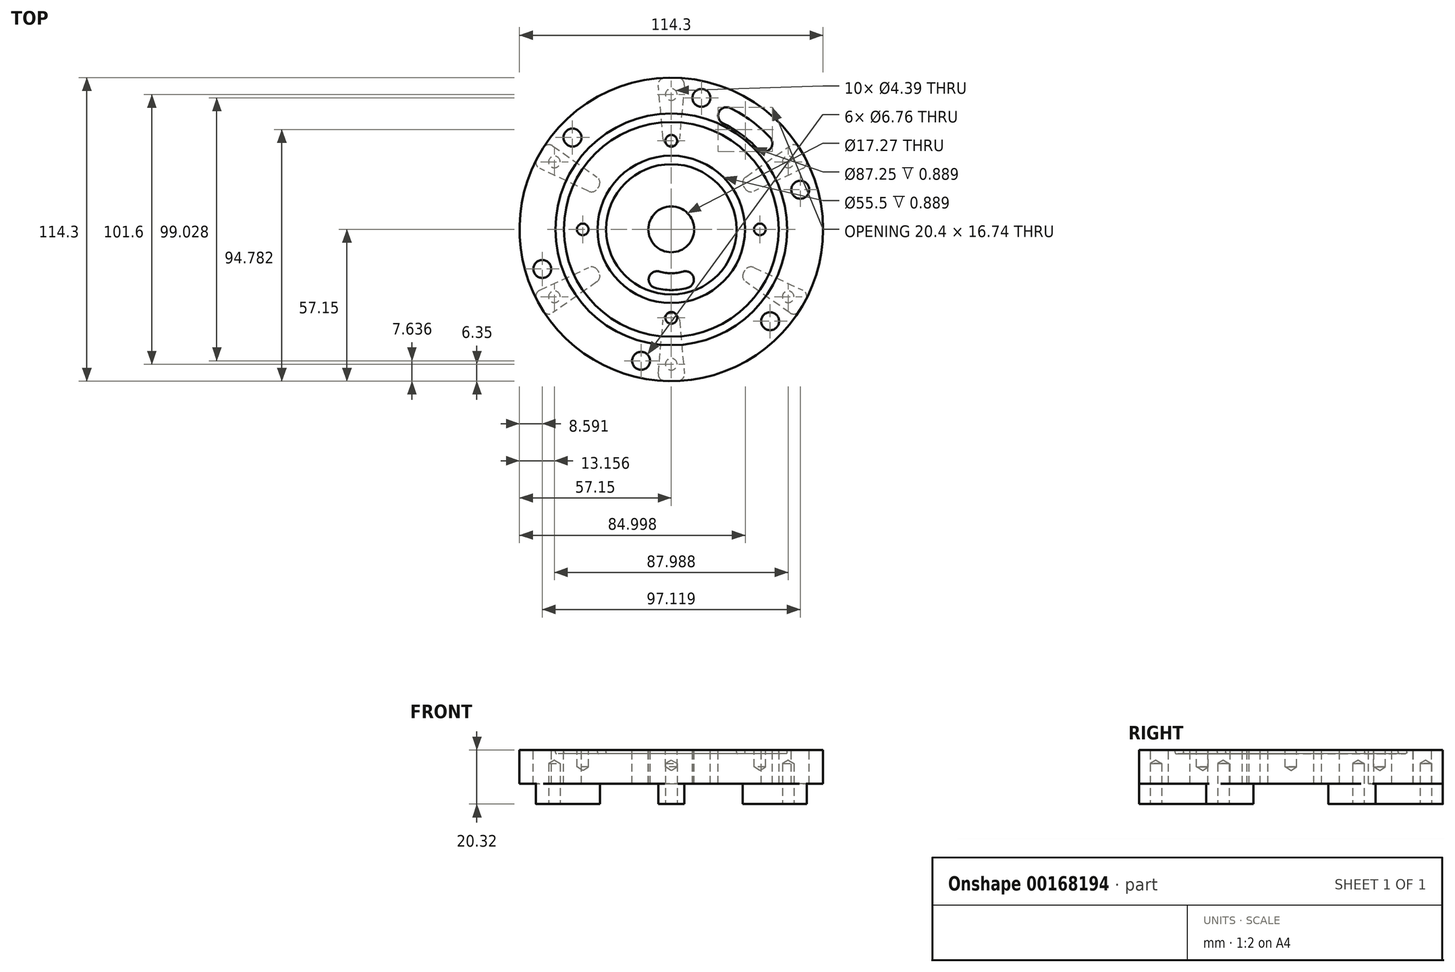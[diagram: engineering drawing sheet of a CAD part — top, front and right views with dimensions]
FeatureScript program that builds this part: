
annotation { "Feature Type Name" : "Feature", "Feature Type Description" : "" }
export const myFeature = defineFeature(function(context is Context, id is Id, definition is map)
    precondition{}
    {
        {
            var Q0;
            Q0=qCreatedBy(makeId("Top.planeOp"),FACE);
            var sketch = newSketch(context, id + "F0", { "sketchPlane" : qUnion([Q0])});
            skCircle(sketch, "E0", {"center": v(0, 0) * mm, "radius": 57.15 * mm});
            skSolve(sketch);
        }
        {
            var Q0;
            Q0=makeQuery(id+"F0.imprint","IMPRINT",FACE,{"disambiguationData":[TD([[makeQuery(id+"F0.imprint","IMPRINT",EDGE,{"derivedFrom":sQuery(id+"F0.wireOp",EDGE,"E0")}),1.0]])]});
            extrude(context, id + "F1", {"entities" : qUnion([Q0]), "depth" : 12.7 * mm});
        }
        {
            var Q0;
            Q0=makeQuery(id+"FNZgXB3MDCEPfWC_1.boolean.opBoolean","SPLIT",FACE,{"disambiguationData":[TD([makeQuery(id+"FNZgXB3MDCEPfWC_1.opExtrude","SWEPT_FACE",FACE,{"disambiguationData":[OSD([sQuery(id+"FiLk9hSRQ8Dv81E_1.wireOp",EDGE,"Xvq2NHEn-EDZK-GzOR-rNrk-moL4fFsD4KvI")])]})])],"derivedFrom":makeQuery(id+"F1.opExtrude","CAP_FACE",FACE,{"disambiguationData":[OSD([sQuery(id+"F0.wireOp",EDGE,"E0")])],"isStart":false})});
            var sketch = newSketch(context, id + "F2", { "sketchPlane" : qUnion([Q0])});
            skCircle(sketch, "E1", {"center": v(0, 0) * mm, "radius": 8.64 * mm});
            skSolve(sketch);
        }
        {
            var Q0;
            Q0 = qSketchRegion(id + "F2", true);
            extrude(context, id + "F3", {"entities" : qUnion([Q0]), "operationType" : NewBodyOperationType.REMOVE, "endBound" : BoundingType.THROUGH_ALL, "oppositeDirection" : true, "depth" : 25.4 * mm});
        }
        {
            var Q0;
            Q0=makeQuery(id+"F1.opExtrude","CAP_FACE",FACE,{"disambiguationData":[OSD([sQuery(id+"F0.wireOp",EDGE,"E0")])],"isStart":true});
            var sketch = newSketch(context, id + "F4", { "sketchPlane" : qUnion([Q0])});
            skArc(sketch, "E2", {"start": v(-5.14, -56.92) * mm, "mid": v(0, -57.15) * mm, "end": v(5.14, -56.92) * mm});
            skArc(sketch, "E3", {"start": v(-2.86, -31.62) * mm, "mid": v(0, -31.75) * mm, "end": v(2.86, -31.62) * mm});
            skLineSegment(sketch, "E4", {"start": v(0, 0) * mm, "end": v(2.86, -31.62) * mm, "construction": true});
            skLineSegment(sketch, "E5", {"start": v(5.14, -56.92) * mm, "end": v(2.86, -31.62) * mm});
            skLineSegment(sketch, "E6", {"start": v(-2.86, -31.62) * mm, "end": v(-5.14, -56.92) * mm});
            skLineSegment(sketch, "E7", {"start": v(-2.86, -31.62) * mm, "end": v(2.86, -31.62) * mm, "construction": true});
            skPoint(sketch, "E8", {"position": v(0, -31.62) * mm});
            skLineSegment(sketch, "E9", {"start": v(0, 0) * mm, "end": v(-2.86, -31.62) * mm, "construction": true});
            skSolve(sketch);
        }
        {
            var Q0;
            Q0 = qSketchRegion(id + "F4", true);
            extrude(context, id + "F5", {"entities" : qUnion([Q0]), "operationType" : NewBodyOperationType.ADD, "depth" : 7.62 * mm});
        }
        {
            var Q0;
            Q0=makeQuery(id+"F5.opExtrude","SWEPT_EDGE",EDGE,{"disambiguationData":[OSD([sQuery(id+"F0.wireOp",EDGE,"E0"),sQuery(id+"F4.wireOp",EDGE,"E2"),sQuery(id+"F4.wireOp",EDGE,"E5")])]});
            var Q1;
            Q1=makeQuery(id+"F5.opExtrude","SWEPT_EDGE",EDGE,{"disambiguationData":[OSD([sQuery(id+"F4.wireOp",EDGE,"E3"),sQuery(id+"F4.wireOp",EDGE,"E5")])]});
            var Q2;
            Q2=makeQuery(id+"F5.opExtrude","SWEPT_EDGE",EDGE,{"disambiguationData":[OSD([sQuery(id+"F0.wireOp",EDGE,"E0"),sQuery(id+"F4.wireOp",EDGE,"E2"),sQuery(id+"F4.wireOp",EDGE,"sxsrdx0H-xiQs-OsdF-6Z6r-2XBd8uqwUAgb")])]});
            var Q3;
            Q3=makeQuery(id+"F5.opExtrude","SWEPT_EDGE",EDGE,{"disambiguationData":[OSD([sQuery(id+"F4.wireOp",EDGE,"E3"),sQuery(id+"F4.wireOp",EDGE,"sxsrdx0H-xiQs-OsdF-6Z6r-2XBd8uqwUAgb")])]});
            fillet(context, id + "F6", {"entities" : qUnion([Q0, Q1, Q2, Q3]), "radius" : 2.54 * mm, "tangentPropagation" : true, "allowEdgeOverflow" : false});
        }
        {
            var Q0;
            Q0=makeQuery(id+"F5.opExtrude","CAP_FACE",FACE,{"disambiguationData":[OSD([sQuery(id+"F4.wireOp",EDGE,"E2"),sQuery(id+"F4.wireOp",EDGE,"E3"),sQuery(id+"F4.wireOp",EDGE,"E5"),sQuery(id+"F4.wireOp",EDGE,"sxsrdx0H-xiQs-OsdF-6Z6r-2XBd8uqwUAgb")])],"isStart":false});
            var sketch = newSketch(context, id + "F7", { "sketchPlane" : qUnion([Q0])});
            skPoint(sketch, "E10", {"position": v(0, -17.36) * mm});
            skLineSegment(sketch, "E11", {"start": v(0, 0) * mm, "end": v(0, -17.36) * mm, "construction": true});
            skLineSegment(sketch, "E12", {"start": v(0, -17.36) * mm, "end": v(0, -57.1) * mm, "construction": true});
            skPoint(sketch, "E13.3.0", {"position": v(0, -50.8) * mm});
            skPoint(sketch, "E13.center", {"position": v(0, 0) * mm});
            skPoint(sketch, "E14.1.0", {"position": v(44, -25.4) * mm});
            skPoint(sketch, "E14.2.0", {"position": v(44, 25.4) * mm});
            skPoint(sketch, "E15.0.3.0", {"position": v(0, 50.8) * mm});
            skPoint(sketch, "E15.0.4.0", {"position": v(-44, 25.4) * mm});
            skPoint(sketch, "E15.0.5.0", {"position": v(-44, -25.4) * mm});
            skSolve(sketch);
        }
        {
            var Q0;
            Q0=makeQuery(id+"F1.opExtrude","SWEPT_BODY",BODY,{"disambiguationData":[OSD([sQuery(id+"F0.wireOp",EDGE,"E0")])]});
            var Q1;
            Q1=makeQuery(id+"F3.boolean.opBoolean","COPY",FACE,{"derivedFrom":makeQuery(id+"F3.opExtrude","SWEPT_FACE",FACE,{"disambiguationData":[OSD([sQuery(id+"F2.wireOp",EDGE,"E1")])]})});
            circularPattern(context, id + "F8", {"operationType" : NewBodyOperationType.ADD, "entities" : qUnion([Q0]), "axis" : qUnion([Q1]), "angle" : 360 * degree, "instanceCount" : 6, "equalSpace" : true});
        }
        {
            var Q0;
            Q0=sQuery(id+"F7.wireOp",VERTEX,"E13.3.0");
            var Q1;
            Q1=sQuery(id+"F7.wireOp",VERTEX,"E14.1.0");
            var Q2;
            Q2=sQuery(id+"F7.wireOp",VERTEX,"E14.2.0");
            var Q3;
            Q3=sQuery(id+"F7.wireOp",VERTEX,"E15.0.3.0");
            var Q4;
            Q4=sQuery(id+"F7.wireOp",VERTEX,"E15.0.4.0");
            var Q5;
            Q5=sQuery(id+"F7.wireOp",VERTEX,"E15.0.5.0");
            var Q6;
            Q6=makeQuery(id+"F1.opExtrude","SWEPT_BODY",BODY,{"disambiguationData":[OSD([sQuery(id+"F0.wireOp",EDGE,"E0")])]});
            hole(context, id + "F9", {"style" : HoleStyle.SIMPLE, "endStyle" : HoleEndStyle.BLIND, "holeDiameter" : 4.4 * mm, "holeDepth" : 15.24 * mm, "locations" : qUnion([Q0, Q1, Q2, Q3, Q4, Q5]), "scope" : qUnion([Q6])});
        }
        {
            var Q0;
            {var subQ0=sQuery(id+"F0.wireOp",EDGE,"E0");Q0=makeQuery(id+"FNZgXB3MDCEPfWC_1.boolean.opBoolean","SPLIT",FACE,{"disambiguationData":[TD([makeQuery(id+"F1.opExtrude","SWEPT_FACE",FACE,{"disambiguationData":[OSD([subQ0])]})])],"derivedFrom":makeQuery(id+"F1.opExtrude","CAP_FACE",FACE,{"disambiguationData":[OSD([subQ0])],"isStart":false})});}
            var sketch = newSketch(context, id + "F10", { "sketchPlane" : qUnion([Q0])});
            skCircle(sketch, "E16", {"center": v(0, 0) * mm, "radius": 42.02 * mm, "construction": true});
            skCircle(sketch, "E17", {"center": v(0, 0) * mm, "radius": 40.42 * mm});
            skCircle(sketch, "E18", {"center": v(0, 0) * mm, "radius": 43.62 * mm});
            skSolve(sketch);
        }
        {
            var Q0;
            Q0 = qSketchRegion(id + "F10", true);
            extrude(context, id + "F11", {"entities" : qUnion([Q0]), "operationType" : NewBodyOperationType.REMOVE, "oppositeDirection" : true, "depth" : 1.3 * mm});
        }
        {
            var Q0;
            Q0=makeQuery(id+"F11.boolean.opBoolean","COPY",EDGE,{"derivedFrom":makeQuery(id+"F11.opExtrude","CAP_EDGE",EDGE,{"disambiguationData":[OSD([sQuery(id+"F10.wireOp",EDGE,"E18")])],"isStart":false})});
            var Q1;
            Q1=makeQuery(id+"F11.boolean.opBoolean","COPY",EDGE,{"derivedFrom":makeQuery(id+"F11.opExtrude","CAP_EDGE",EDGE,{"disambiguationData":[OSD([sQuery(id+"F10.wireOp",EDGE,"E17")])],"isStart":false})});
            fillet(context, id + "F12", {"entities" : qUnion([Q0, Q1]), "radius" : 0.4 * mm, "tangentPropagation" : true, "allowEdgeOverflow" : false});
        }
        {
            var Q0;
            {var subQ0=sQuery(id+"F0.wireOp",EDGE,"E0");var subQ1=makeQuery(id+"F1.opExtrude","SWEPT_FACE",FACE,{"disambiguationData":[OSD([subQ0])]});Q0=makeQuery(id+"F11.boolean.opBoolean","SPLIT",FACE,{"disambiguationData":[TD([subQ1])],"derivedFrom":makeQuery(id+"FNZgXB3MDCEPfWC_1.boolean.opBoolean","SPLIT",FACE,{"disambiguationData":[TD([subQ1])],"derivedFrom":makeQuery(id+"F1.opExtrude","CAP_FACE",FACE,{"disambiguationData":[OSD([subQ0])],"isStart":false})})});}
            var sketch = newSketch(context, id + "F13", { "sketchPlane" : qUnion([Q0])});
            skArc(sketch, "E19", {"start": v(33.85, 27.51) * mm, "mid": v(25.95, 35.07) * mm, "end": v(16.41, 40.42) * mm, "construction": true});
            skArc(sketch, "E20.0", {"start": v(34.5, 28.03) * mm, "mid": v(26.44, 35.73) * mm, "end": v(16.72, 41.19) * mm});
            skArc(sketch, "E21", {"start": v(39.42, 32.04) * mm, "mid": v(30.22, 40.84) * mm, "end": v(19.1, 47.07) * mm});
            skLineSegment(sketch, "E22", {"start": v(33.85, 27.51) * mm, "end": v(34.5, 28.03) * mm, "construction": true});
            skLineSegment(sketch, "E23", {"start": v(39.42, 32.04) * mm, "end": v(34.5, 28.03) * mm});
            skLineSegment(sketch, "E24", {"start": v(0, 0) * mm, "end": v(33.85, 27.51) * mm, "construction": true});
            skLineSegment(sketch, "E25", {"start": v(16.41, 40.42) * mm, "end": v(16.72, 41.19) * mm, "construction": true});
            skLineSegment(sketch, "E26", {"start": v(19.1, 47.07) * mm, "end": v(16.72, 41.19) * mm});
            skLineSegment(sketch, "E27", {"start": v(16.41, 40.42) * mm, "end": v(0, 0) * mm, "construction": true});
            skCircle(sketch, "E28.0", {"center": v(0, 50.8) * mm, "radius": 2.2 * mm, "construction": true});
            skCircle(sketch, "E28.1", {"center": v(44, 25.4) * mm, "radius": 2.2 * mm, "construction": true});
            skLineSegment(sketch, "E29", {"start": v(0, 0) * mm, "end": v(0, 50.8) * mm, "construction": true});
            skLineSegment(sketch, "E30", {"start": v(44, 25.4) * mm, "end": v(0, 0) * mm, "construction": true});
            skSolve(sketch);
        }
        {
            var Q0;
            Q0 = qSketchRegion(id + "F13", true);
            extrude(context, id + "F14", {"entities" : qUnion([Q0]), "operationType" : NewBodyOperationType.REMOVE, "endBound" : BoundingType.THROUGH_ALL, "oppositeDirection" : true, "depth" : 25.4 * mm});
        }
        {
            var Q0;
            Q0=makeQuery(id+"F14.boolean.opBoolean","COPY",EDGE,{"derivedFrom":makeQuery(id+"F14.opExtrude","SWEPT_EDGE",EDGE,{"disambiguationData":[OSD([sQuery(id+"F13.wireOp",EDGE,"E21"),sQuery(id+"F13.wireOp",EDGE,"E23")])]})});
            var Q1;
            Q1=makeQuery(id+"F14.boolean.opBoolean","COPY",EDGE,{"derivedFrom":makeQuery(id+"F14.opExtrude","SWEPT_EDGE",EDGE,{"disambiguationData":[OSD([sQuery(id+"F13.wireOp",EDGE,"E21"),sQuery(id+"F13.wireOp",EDGE,"E26")])]})});
            var Q2;
            Q2=makeQuery(id+"F14.boolean.opBoolean","COPY",EDGE,{"derivedFrom":makeQuery(id+"F14.opExtrude","SWEPT_EDGE",EDGE,{"disambiguationData":[OSD([sQuery(id+"F13.wireOp",EDGE,"E20.0"),sQuery(id+"F13.wireOp",EDGE,"E26")])]})});
            var Q3;
            Q3=makeQuery(id+"F14.boolean.opBoolean","COPY",EDGE,{"derivedFrom":makeQuery(id+"F14.opExtrude","SWEPT_EDGE",EDGE,{"disambiguationData":[OSD([sQuery(id+"F13.wireOp",EDGE,"E20.0"),sQuery(id+"F13.wireOp",EDGE,"E23")])]})});
            fillet(context, id + "F15", {"entities" : qUnion([Q0, Q1, Q2, Q3]), "radius" : 3.17 * mm, "tangentPropagation" : true, "allowEdgeOverflow" : false});
        }
        {
            var Q0;
            Q0=makeQuery(id+"F11.boolean.opBoolean","SPLIT",FACE,{"disambiguationData":[TD([makeQuery(id+"F3.boolean.opBoolean","COPY",FACE,{"derivedFrom":makeQuery(id+"F3.opExtrude","SWEPT_FACE",FACE,{"disambiguationData":[OSD([sQuery(id+"F2.wireOp",EDGE,"E1")])]})})])],"derivedFrom":makeQuery(id+"F1.opExtrude","CAP_FACE",FACE,{"disambiguationData":[OSD([sQuery(id+"F0.wireOp",EDGE,"E0")])],"isStart":false})});
            var sketch = newSketch(context, id + "F16", { "sketchPlane" : qUnion([Q0])});
            skCircle(sketch, "E31", {"center": v(0, 0) * mm, "radius": 26.15 * mm, "construction": true});
            skCircle(sketch, "E32", {"center": v(0, 0) * mm, "radius": 24.55 * mm});
            skCircle(sketch, "E33", {"center": v(0, 0) * mm, "radius": 27.75 * mm});
            skSolve(sketch);
        }
        {
            var Q0;
            Q0 = qSketchRegion(id + "F16", true);
            extrude(context, id + "F17", {"entities" : qUnion([Q0]), "operationType" : NewBodyOperationType.REMOVE, "oppositeDirection" : true, "depth" : 1.3 * mm});
        }
        {
            var Q0;
            Q0=makeQuery(id+"F17.boolean.opBoolean","COPY",EDGE,{"derivedFrom":makeQuery(id+"F17.opExtrude","CAP_EDGE",EDGE,{"disambiguationData":[OSD([sQuery(id+"F16.wireOp",EDGE,"E33")])],"isStart":false})});
            var Q1;
            Q1=makeQuery(id+"F17.boolean.opBoolean","COPY",EDGE,{"derivedFrom":makeQuery(id+"F17.opExtrude","CAP_EDGE",EDGE,{"disambiguationData":[OSD([sQuery(id+"F16.wireOp",EDGE,"E32")])],"isStart":false})});
            fillet(context, id + "F18", {"entities" : qUnion([Q0, Q1]), "radius" : 0.4 * mm, "tangentPropagation" : true, "allowEdgeOverflow" : false});
        }
        {
            var Q0;
            {var subQ0=makeQuery(id+"F3.boolean.opBoolean","COPY",FACE,{"derivedFrom":makeQuery(id+"F3.opExtrude","SWEPT_FACE",FACE,{"disambiguationData":[OSD([sQuery(id+"F2.wireOp",EDGE,"E1")])]})});Q0=makeQuery(id+"F17.boolean.opBoolean","SPLIT",FACE,{"disambiguationData":[TD([subQ0])],"derivedFrom":makeQuery(id+"F11.boolean.opBoolean","SPLIT",FACE,{"disambiguationData":[TD([subQ0])],"derivedFrom":makeQuery(id+"F1.opExtrude","CAP_FACE",FACE,{"disambiguationData":[OSD([sQuery(id+"F0.wireOp",EDGE,"E0")])],"isStart":false})})});}
            var sketch = newSketch(context, id + "F19", { "sketchPlane" : qUnion([Q0])});
            skLineSegment(sketch, "E34", {"start": v(0, 0) * mm, "end": v(6.98, -14.96) * mm, "construction": true});
            skArc(sketch, "E35", {"start": v(6.98, -14.96) * mm, "mid": v(0, -16.51) * mm, "end": v(-6.98, -14.96) * mm});
            skArc(sketch, "E36", {"start": v(9.66, -20.72) * mm, "mid": v(0, -22.86) * mm, "end": v(-9.66, -20.72) * mm});
            skLineSegment(sketch, "E37", {"start": v(-9.66, -20.72) * mm, "end": v(-6.98, -14.96) * mm});
            skLineSegment(sketch, "E38", {"start": v(0, 0) * mm, "end": v(-6.98, -14.96) * mm, "construction": true});
            skLineSegment(sketch, "E39", {"start": v(9.66, -20.72) * mm, "end": v(6.98, -14.96) * mm});
            skLineSegment(sketch, "E40", {"start": v(0, -16.51) * mm, "end": v(0, 0) * mm, "construction": true});
            skSolve(sketch);
        }
        {
            var Q0;
            Q0 = qSketchRegion(id + "F19", true);
            extrude(context, id + "F20", {"entities" : qUnion([Q0]), "operationType" : NewBodyOperationType.REMOVE, "endBound" : BoundingType.THROUGH_ALL, "oppositeDirection" : true, "depth" : 25.4 * mm});
        }
        {
            var Q0;
            Q0=makeQuery(id+"F20.boolean.opBoolean","COPY",EDGE,{"derivedFrom":makeQuery(id+"F20.opExtrude","SWEPT_EDGE",EDGE,{"disambiguationData":[OSD([sQuery(id+"F19.wireOp",EDGE,"E35"),sQuery(id+"F19.wireOp",EDGE,"E37")])]})});
            var Q1;
            Q1=makeQuery(id+"F20.boolean.opBoolean","COPY",EDGE,{"derivedFrom":makeQuery(id+"F20.opExtrude","SWEPT_EDGE",EDGE,{"disambiguationData":[OSD([sQuery(id+"F19.wireOp",EDGE,"E36"),sQuery(id+"F19.wireOp",EDGE,"E37")])]})});
            var Q2;
            Q2=makeQuery(id+"F20.boolean.opBoolean","COPY",EDGE,{"derivedFrom":makeQuery(id+"F20.opExtrude","SWEPT_EDGE",EDGE,{"disambiguationData":[OSD([sQuery(id+"F19.wireOp",EDGE,"E35"),sQuery(id+"F19.wireOp",EDGE,"nJm0js4g-YAOA-XNub-Ppl5-B8IrQimasCNu")])]})});
            var Q3;
            Q3=makeQuery(id+"F20.boolean.opBoolean","COPY",EDGE,{"derivedFrom":makeQuery(id+"F20.opExtrude","SWEPT_EDGE",EDGE,{"disambiguationData":[OSD([sQuery(id+"F19.wireOp",EDGE,"E36"),sQuery(id+"F19.wireOp",EDGE,"nJm0js4g-YAOA-XNub-Ppl5-B8IrQimasCNu")])]})});
            fillet(context, id + "F21", {"entities" : qUnion([Q0, Q1, Q2, Q3]), "radius" : 3.17 * mm, "tangentPropagation" : true, "allowEdgeOverflow" : false});
        }
        {
            var Q0;
            {var subQ0=makeQuery(id+"F11.opExtrude","SWEPT_FACE",FACE,{"disambiguationData":[OSD([sQuery(id+"F10.wireOp",EDGE,"E17")])]});Q0=makeQuery(id+"F17.boolean.opBoolean","SPLIT",FACE,{"disambiguationData":[TD([makeQuery(id+"F11.boolean.opBoolean","COPY",FACE,{"derivedFrom":subQ0})])],"derivedFrom":makeQuery(id+"F11.boolean.opBoolean","SPLIT",FACE,{"disambiguationData":[TD([makeQuery(id+"F3.boolean.opBoolean","COPY",FACE,{"derivedFrom":makeQuery(id+"F3.opExtrude","SWEPT_FACE",FACE,{"disambiguationData":[OSD([sQuery(id+"F2.wireOp",EDGE,"E1")])]})})])],"derivedFrom":makeQuery(id+"F1.opExtrude","CAP_FACE",FACE,{"disambiguationData":[OSD([sQuery(id+"F0.wireOp",EDGE,"E0")])],"isStart":false})})});}
            var sketch = newSketch(context, id + "F22", { "sketchPlane" : qUnion([Q0])});
            skCircle(sketch, "E41", {"center": v(0, 0) * mm, "radius": 33.34 * mm, "construction": true});
            skLineSegment(sketch, "E42", {"start": v(0, 0) * mm, "end": v(0, -33.34) * mm, "construction": true});
            skPoint(sketch, "E43", {"position": v(0, -33.34) * mm});
            skPoint(sketch, "E44", {"position": v(-33.34, 0) * mm});
            skPoint(sketch, "E45", {"position": v(33.34, 0) * mm});
            skPoint(sketch, "E46", {"position": v(0, 33.34) * mm});
            skSolve(sketch);
        }
        {
            var Q0;
            Q0=sQuery(id+"F22.wireOp",VERTEX,"E44");
            var Q1;
            Q1=sQuery(id+"F22.wireOp",VERTEX,"E43");
            var Q2;
            Q2=sQuery(id+"F22.wireOp",VERTEX,"E45");
            var Q3;
            Q3=sQuery(id+"F22.wireOp",VERTEX,"E46");
            var Q4;
            Q4=makeQuery(id+"F1.opExtrude","SWEPT_BODY",BODY,{"disambiguationData":[OSD([sQuery(id+"F0.wireOp",EDGE,"E0")])]});
            hole(context, id + "F23", {"style" : HoleStyle.SIMPLE, "endStyle" : HoleEndStyle.BLIND, "holeDiameter" : 4.4 * mm, "holeDepth" : 6.35 * mm, "locations" : qUnion([Q0, Q1, Q2, Q3]), "scope" : qUnion([Q4])});
        }
        {
            var Q0;
            {var subQ1=sQuery(id+"F0.wireOp",EDGE,"E0");var subQ2=makeQuery(id+"F1.opExtrude","SWEPT_FACE",FACE,{"disambiguationData":[OSD([subQ1])]});Q0=makeQuery(id+"F11.boolean.opBoolean","SPLIT",FACE,{"disambiguationData":[TD([subQ2])],"derivedFrom":makeQuery(id+"F1.opExtrude","CAP_FACE",FACE,{"disambiguationData":[OSD([subQ1])],"isStart":false})});}
            var sketch = newSketch(context, id + "F24", { "sketchPlane" : qUnion([Q0])});
            skLineSegment(sketch, "E47", {"start": v(0, 0) * mm, "end": v(11.36, 49.51) * mm, "construction": true});
            skPoint(sketch, "E48", {"position": v(11.36, 49.51) * mm});
            skPoint(sketch, "E49.1.0", {"position": v(-37.2, 34.6) * mm});
            skPoint(sketch, "E49.2.0", {"position": v(-48.56, -14.92) * mm});
            skPoint(sketch, "E49.3.0", {"position": v(-11.36, -49.51) * mm});
            skPoint(sketch, "E49.4.0", {"position": v(37.2, -34.6) * mm});
            skPoint(sketch, "E49.5.0", {"position": v(48.56, 14.92) * mm});
            skPoint(sketch, "E49.center", {"position": v(0, 0) * mm});
            skSolve(sketch);
        }
        {
            var Q0;
            Q0=sQuery(id+"F24.wireOp",VERTEX,"E48");
            var Q1;
            Q1=sQuery(id+"F24.wireOp",VERTEX,"E49.5.0");
            var Q2;
            Q2=sQuery(id+"F24.wireOp",VERTEX,"E49.4.0");
            var Q3;
            Q3=sQuery(id+"F24.wireOp",VERTEX,"E49.3.0");
            var Q4;
            Q4=sQuery(id+"F24.wireOp",VERTEX,"E49.2.0");
            var Q5;
            Q5=sQuery(id+"F24.wireOp",VERTEX,"E49.1.0");
            var Q6;
            Q6=makeQuery(id+"F1.opExtrude","SWEPT_BODY",BODY,{"disambiguationData":[OSD([sQuery(id+"F0.wireOp",EDGE,"E0")])]});
            hole(context, id + "F25", {"style" : HoleStyle.SIMPLE, "endStyle" : HoleEndStyle.THROUGH, "holeDiameter" : 6.76 * mm, "locations" : qUnion([Q0, Q1, Q2, Q3, Q4, Q5]), "scope" : qUnion([Q6]), "isTappedThrough" : true});
        }
    });
